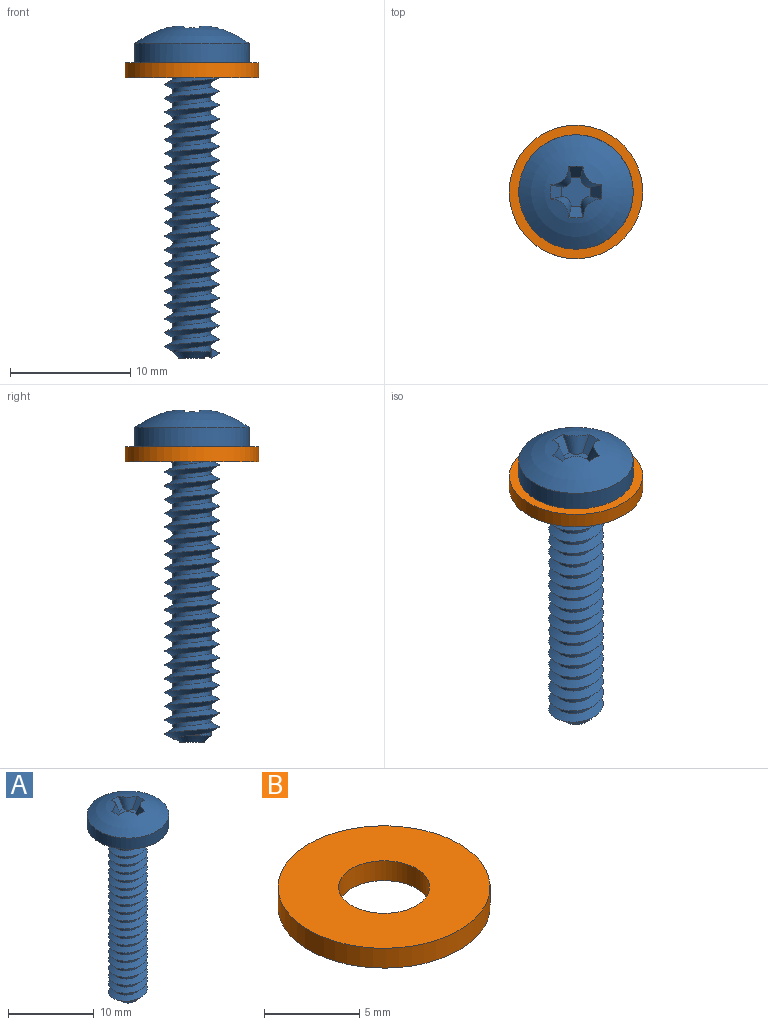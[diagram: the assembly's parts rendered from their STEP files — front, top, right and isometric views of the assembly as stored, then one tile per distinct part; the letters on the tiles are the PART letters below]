
ASSEMBLY  parts=2 mates=1
PART A: 21 faces, bbox 9.7x9.7x27.9 mm
  f0: cylinder r=1.59mm len=23.59mm, axis (0,0,1), area 90.5mm2, adj f1,f6,f8,f10,f11
  f1: torus R=2.1mm, axis (0,0,-1), area 6.1mm2, adj f0,f4,f7,f8
  f2: cylinder r=4.76mm len=9.53mm, axis (0,0,-1), area 47.5mm2, adj f3,f4
  f3: sphere r=7.94mm, area 68.1mm2, adj f2,f13,f14,f15,f16,f17,f18,f19
  f4: plane 9.53x9.53mm, normal (0,0,-1), area 57.5mm2, adj f1,f2
  f5: plane 2.16x2.16mm, normal (0,0,-1), area 3.7mm2, adj f6
  f6: cone r=1.08mm half-angle=45deg, axis (0,0,1), area 6mm2, adj f0,f5,f9
  f7: plane 0.69x0.51mm, normal (0,1,0), area 0.1mm2, adj f1,f8,f11
  f8: bspline ~24.5x5.25mm, area 199.7mm2, adj f0,f1,f7,f10,f11
  f9: cylinder r=1.59mm len=3.07mm, axis (0,0,1), area 1.1mm2, adj f6,f10,f11
  f10: plane 0.79x0.69mm, normal (0,-1,0), area 0.3mm2, adj f0,f8,f9,f11
  f11: bspline ~24.5x5.25mm, area 203mm2, adj f0,f7,f8,f9,f10
  f12: plane 2.38x2.38mm, normal (0,0,1), area 3.6mm2, adj f13,f14,f15,f16,f17,f18,f19,f20
  f13: plane 1.43x1.31mm, normal (0,-0.8,0.6), area 1.6mm2, adj f3,f12,f14,f20
  f14: bspline ~1.98x1.98mm, area 2.5mm2, adj f3,f12,f13,f15
  f15: plane 1.29x1.17mm, normal (-0.8,0,0.6), area 1.6mm2, adj f3,f12,f14,f16
  f16: bspline ~1.98x1.98mm, area 2.5mm2, adj f3,f12,f15,f17
  f17: plane 1.43x1.31mm, normal (0,0.8,0.6), area 1.6mm2, adj f3,f12,f16,f18
  f18: bspline ~1.98x1.98mm, area 2.5mm2, adj f3,f12,f17,f19
  f19: plane 1.43x1.31mm, normal (0.8,0,0.6), area 1.6mm2, adj f3,f12,f18,f20
  f20: bspline ~1.98x1.98mm, area 2.5mm2, adj f3,f12,f13,f19
PART B: 4 faces, bbox 11.1x11.1x1.3 mm
  f0: cylinder r=2.38mm len=4.76mm, axis (0,0,-1), area 19mm2, adj f2,f3
  f1: cylinder r=5.56mm len=11.11mm, axis (0,0,-1), area 44.3mm2, adj f2,f3
  f2: plane 11.11x11.11mm, normal (0,0,1), area 79.2mm2, adj f0,f1
  f3: plane 11.11x11.11mm, normal (0,0,-1), area 79.2mm2, adj f0,f1
PLACE A t=(0,0,26.19)mm
PLACE B t=(0,0,23.97)mm
MATE fastened A.f2 <-> B.f1  axis (0,0,-1) through (0,0,24.61)mm
